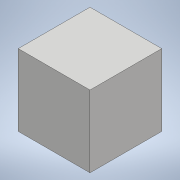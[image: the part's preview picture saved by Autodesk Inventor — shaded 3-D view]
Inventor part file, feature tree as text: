
AUTODESK INVENTOR PART (.ipt)
format: ipt  version: 2020.2 (Build 242310000, 310)  size: 78,848 bytes
history: native  units: mm
features: other x1, extrude x1, sketch x1
ambient origin geometry x8: Origin, YZ Plane, XZ Plane, XY Plane, X Axis, Y Axis, Z Axis, Center Point
bodies: Body1 (feature_tree)
feature tree (3):
  other  "ソリッド1"
  extrude  "押し出し1"  Depth=30.0mm TaperAngle=0.0deg
  sketch  "スケッチ1"
